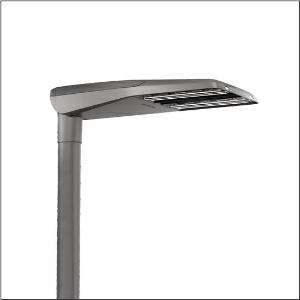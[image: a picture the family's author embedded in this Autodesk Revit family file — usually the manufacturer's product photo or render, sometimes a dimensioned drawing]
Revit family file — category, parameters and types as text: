
# Revit family: streetlight_sl_11_iq_midi___st1_0a_5xc3m51f08le_689c
name_source: partatom
category: Lighting Fixtures
units: mm (PartAtom-declared; Revit-internal decimal feet)

## family parameters
Cut with Voids When Loaded = No
Host = Face
Light Source = No
Part Type = Normal
Room Calculation Point = No
Round Connector Dimension = Use Diameter
Shared = No

## types (1)
- --- (1 x LED, 8920 lm, 60.4 W, 3000K)
    Apparent Load = 60 VA
    CIE Flux Codes = 33 66 96 100 100
    Color Rendering = 70
    Color Temperature = 3000K
    Default Elevation = 1800 mm
    Description = Streetlight SL 11 iQ midi, mast luminaire, primary light control with 3 zone facetted reflector, of plastic, silver coated, highly specular, primary optical cover: cover, of PMMA, transparent, light distribution: ST1.0a, light emission: direct distribution, primary light characteristic: asymmetric, installation type: post-top, side-entry, LED, High Power LED, rated luminous flux: 8.920lm, luminous efficacy: 148lm/W, light colour: 730, colour temperature: 3000K, control: optimised constant luminous flux control (CLO 2.0), Street-Remote, Desk-Remote (wireless, voltage-free reading and setting of iQ features in the workshop via application-optimized NFC function/RFID function), Light-Fading, Smart-Wire, Night-Set, Lumen-Switch, Temp-Guard, Auto-Match, with cable H07RN-F 5x 1.5mm², mains connection: 230..240V, AC, 50/60Hz, connection cable pre-assembled, cable length: 8,5m, start of lifetime: 60W, end of service life: 63W, reduction: 30W, luminaire housing, of diecast aluminium, powder-coated, Siteco® metallic grey (DB 702S), please order mast flange separately, inclination adjustable without tools: 0°, 5°, 10°, 15° (post-top) | 0°, -5°, -10°, -15° (side-entry), sealing non-destructively replaceable, multi-level sealing system, length: 780mm, width: 376mm, height: 118mm, mast flange for spigot size: 42mm (side-entry): 5XC10008XM4, 60/48mm (side-entry/post-top): 5XC10108XM2, 76/60mm (side-entry/post-top): 5XC10108XM1, equipment: standard, protection rating (complete): IP66, insulation class (complete): insulation class II (safety insulation), certification: CE, ENEC, VDE, impact resistance: IK09, permissible operating ambient temperature for outdoor applications: -25..+50°C, standard-compliant lighting for roads and squares, Environmental Product Declaration (EPD) tested and certified by an independent institute, packaging unit: 1 piece

Light Distribution: ST1.0a
    Height = 118 mm
    Lamp = 1 x LED
    Lamp Light Flux = 8920 lm
    Lamp Power = 60.4 W
    Lamp count = 1
    Length = 780 mm
    Luminous efficacy = 148 lm/W
    Manufacturer = Siteco
    ModVariant = No
    Model = 5XC3M51F08LE
    Number of Poles = 1
    OnlyDefault = Yes
    Power Factor = 1
    Product Name = Streetlight SL 11 iQ midi | ST1.0a
    Product group = mast luminaire | pylon top
    ProductGroupID = 6100
    Protection Class = Protection class II
    Protection Degree = IP 66
    RLX_Detail_Level = 1
    RLX_Emergency_Light_Flux = 0 lm
    RLX_Emergency_Type = 0
    RLX_Emergency_Type_DB = No
    RlxData = <blob elided: 69973 chars, md5=25cceb79>
    Socket = socket
    Standby Power = 0 W
    System Light Flux = 8920 lm
    System Power = 60 W
    Type Comments = factory setting: luminous flux: 100 % | dim-lin: 254 | 520 mA
    Type Image = l_1005960.jpg
    URL = http://relux.com
    VarID = @adj_039493
    Voltage = 0 V
    Weight = 0.00 kg
    Width = 376 mm

## geometry (parser evidence)
native form markers: Blend x4, Sweep x11
no freeform markers — native parametric forms only
